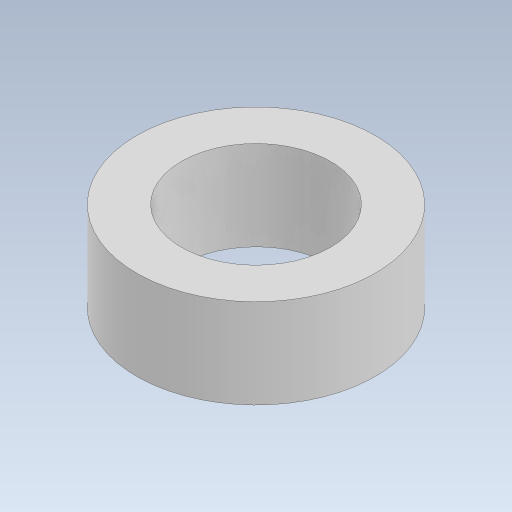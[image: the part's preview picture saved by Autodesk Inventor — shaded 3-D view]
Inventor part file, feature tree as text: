
AUTODESK INVENTOR PART (.ipt)
format: ipt  version: 2023.5 (Build 275446000, 446)  size: 92,672 bytes
history: native  units: mm
features: extrude x1, sketch x1
ambient origin geometry x8: Origin, YZ Plane, XZ Plane, XY Plane, X Axis, Y Axis, Z Axis, Center Point
bodies: Solid1 (feature_tree)
feature tree (2):
  extrude  "Extrusion1"  Depth=3.0mm
  sketch  "Sketch1"  dims[d0=5.0mm d1=8.0mm d2=3.0mm d3=0.0mm]
